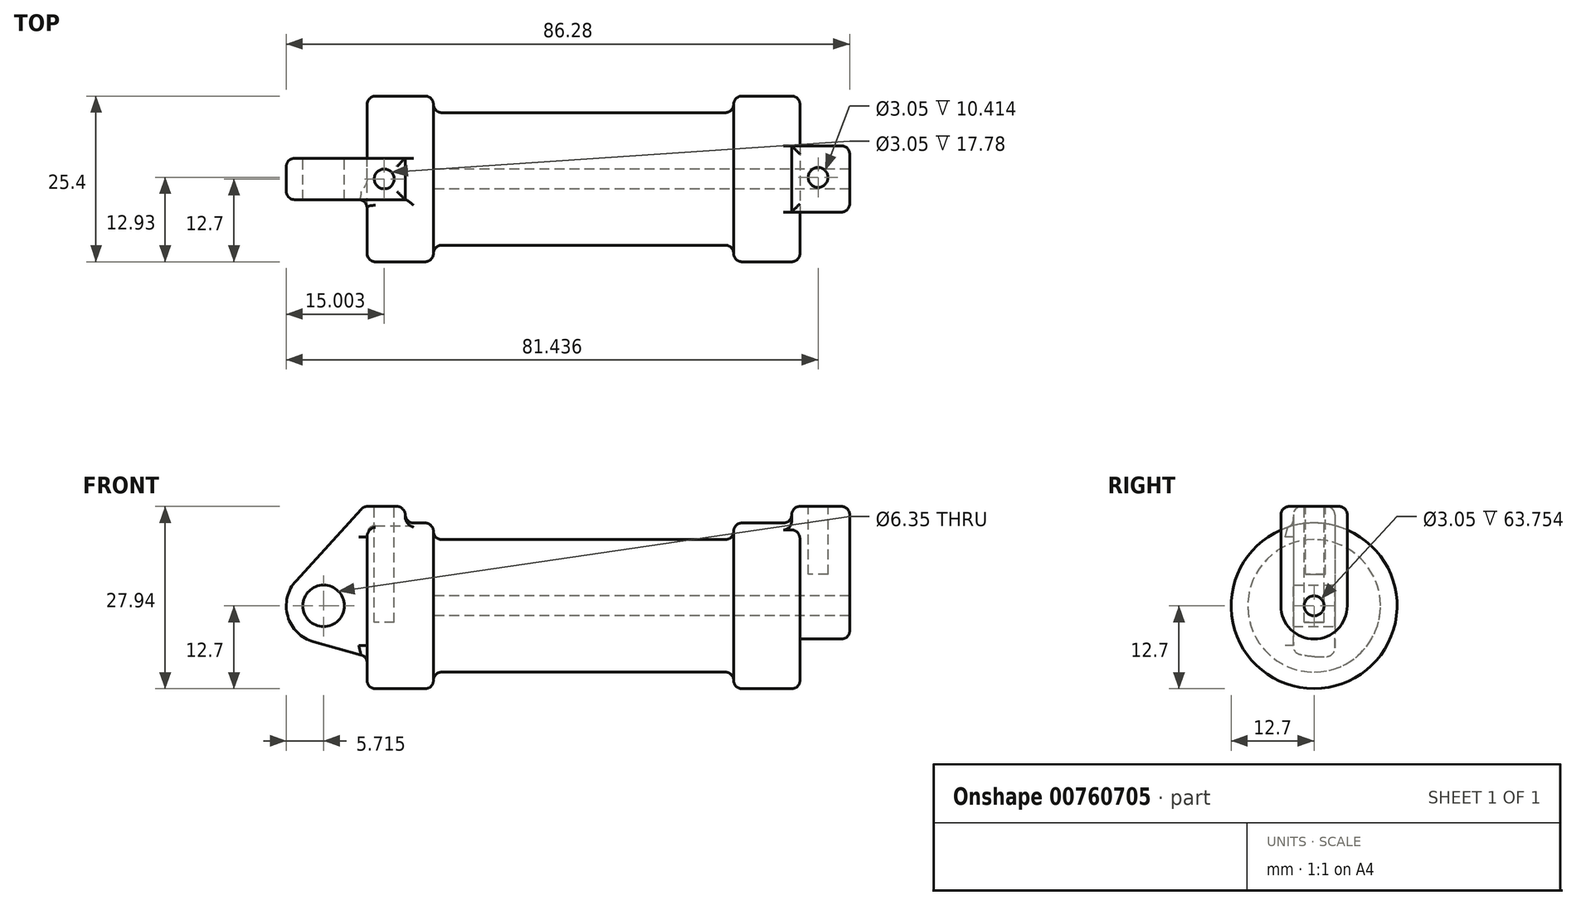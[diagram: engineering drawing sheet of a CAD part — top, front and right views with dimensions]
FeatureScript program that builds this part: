
annotation { "Feature Type Name" : "Feature", "Feature Type Description" : "" }
export const myFeature = defineFeature(function(context is Context, id is Id, definition is map)
    precondition{}
    {
        {
            var Q0;
            Q0=qCreatedBy(makeId("Front.planeOp"),FACE);
            var sketch = newSketch(context, id + "F0", { "sketchPlane" : qUnion([Q0])});
            skLineSegment(sketch, "E0", {"start": v(0, 0) * mm, "end": v(0, 12.7) * mm});
            skLineSegment(sketch, "E1", {"start": v(0, 12.7) * mm, "end": v(10.16, 12.7) * mm});
            skLineSegment(sketch, "E2", {"start": v(10.16, 12.7) * mm, "end": v(10.16, 10.16) * mm});
            skLineSegment(sketch, "E3", {"start": v(10.16, 10.16) * mm, "end": v(56.13, 10.16) * mm});
            skLineSegment(sketch, "E4", {"start": v(56.13, 10.16) * mm, "end": v(56.13, 12.7) * mm});
            skLineSegment(sketch, "E5", {"start": v(56.13, 12.7) * mm, "end": v(66.3, 12.7) * mm});
            skLineSegment(sketch, "E6", {"start": v(66.3, 12.7) * mm, "end": v(66.3, 0) * mm});
            skLineSegment(sketch, "E7", {"start": v(66.3, 0) * mm, "end": v(0, 0) * mm});
            skLineSegment(sketch, "E8", {"start": v(5.84, 15.24) * mm, "end": v(-0.5, 15.24) * mm});
            skLineSegment(sketch, "E9", {"start": v(-0.5, 15.24) * mm, "end": v(-10.88, 3.85) * mm});
            skLineSegment(sketch, "E10", {"start": v(0, 0) * mm, "end": v(-6.65, 0) * mm});
            skCircle(sketch, "E11", {"center": v(-6.65, 0) * mm, "radius": 5.72 * mm});
            skCircle(sketch, "E12", {"center": v(-6.65, 0) * mm, "radius": 3.18 * mm});
            skLineSegment(sketch, "E13", {"start": v(5.84, 15.24) * mm, "end": v(5.84, -9.4) * mm});
            skLineSegment(sketch, "E14", {"start": v(5.84, -9.4) * mm, "end": v(-8.18, -5.5) * mm});
            skSolve(sketch);
        }
        {
            var Q0;
            {var subQ0=sQuery(id+"F0.wireOp",EDGE,"E2");Q0=makeQuery(id+"F0.imprint","IMPRINT",FACE,{"disambiguationData":[TD([[makeQuery(id+"F0.imprint","IMPRINT",EDGE,{"derivedFrom":subQ0}),-1.0]])]});}
            var Q1;
            {var subQ0=sQuery(id+"F0.wireOp",EDGE,"E0");Q1=makeQuery(id+"F0.imprint","IMPRINT",FACE,{"disambiguationData":[TD([[makeQuery(id+"F0.imprint","IMPRINT",EDGE,{"derivedFrom":subQ0}),-1.0]])]});}
            var Q2;
            Q2=sQuery(id+"F0.wireOp",EDGE,"E7");
            revolve(context, id + "F1", {"surfaceOperationType" : NewSurfaceOperationType.NEW, "entities" : qUnion([Q0, Q1]), "axis" : qUnion([Q2]), "revolveType" : RevolveType.FULL});
        }
        {
            var Q0;
            {var subQ5=sQuery(id+"F0.wireOp",EDGE,"E12");Q0=makeQuery(id+"F0.imprint","IMPRINT",FACE,{"disambiguationData":[TD([[makeQuery(id+"F0.imprint","IMPRINT",EDGE,{"derivedFrom":subQ5}),-1.0]])]});}
            var Q1;
            {var subQ0=sQuery(id+"F0.wireOp",EDGE,"E14");Q1=makeQuery(id+"F0.imprint","IMPRINT",FACE,{"disambiguationData":[TD([[makeQuery(id+"F0.imprint","IMPRINT",EDGE,{"derivedFrom":subQ0}),-1.0]])]});}
            var Q2;
            {var subQ0=sQuery(id+"F0.wireOp",EDGE,"E0");Q2=makeQuery(id+"F0.imprint","IMPRINT",FACE,{"disambiguationData":[TD([[makeQuery(id+"F0.imprint","IMPRINT",EDGE,{"derivedFrom":subQ0}),-1.0]])]});}
            var Q3;
            {var subQ1=sQuery(id+"F0.wireOp",EDGE,"E0");Q3=makeQuery(id+"F0.imprint","IMPRINT",FACE,{"disambiguationData":[TD([[makeQuery(id+"F0.imprint","IMPRINT",EDGE,{"derivedFrom":subQ1}),1.0]])]});}
            extrude(context, id + "F2", {"entities" : qUnion([Q0, Q1, Q2, Q3]), "endBound" : BoundingType.SYMMETRIC, "depth" : 6.35 * mm, "offsetDistance" : 25.4 * mm});
        }
        {
            var Q0;
            Q0=makeQuery(id+"F1.opRevolve","SWEPT_FACE",FACE,{"disambiguationData":[OSD([sQuery(id+"F0.wireOp",EDGE,"E6")])]});
            var sketch = newSketch(context, id + "F3", { "sketchPlane" : qUnion([Q0])});
            skCircle(sketch, "E15", {"center": v(0, 0) * mm, "radius": 1.52 * mm});
            skCircle(sketch, "E16", {"center": v(0, 0) * mm, "radius": 5.08 * mm});
            skLineSegment(sketch, "E17", {"start": v(-5.08, 0) * mm, "end": v(-5.08, 15.24) * mm});
            skLineSegment(sketch, "E18", {"start": v(-5.08, 15.24) * mm, "end": v(5.08, 15.24) * mm});
            skLineSegment(sketch, "E19", {"start": v(5.08, 15.24) * mm, "end": v(5.08, 0) * mm});
            skSolve(sketch);
        }
        {
            var Q0;
            {var subQ0=sQuery(id+"F3.wireOp",EDGE,"E18");Q0=makeQuery(id+"F3.imprint","IMPRINT",FACE,{"disambiguationData":[TD([[makeQuery(id+"F3.imprint","IMPRINT",EDGE,{"derivedFrom":subQ0}),-1.0]])]});}
            var Q1;
            {var subQ0=sQuery(id+"F3.wireOp",EDGE,"E17");var subQ1=sQuery(id+"F3.wireOp",EDGE,"E16");var subQ2=makeQuery(id+"F3.imprint","INTERSECT",VERTEX,{"derivedFrom":[subQ1,subQ0]});Q1=makeQuery(id+"F3.imprint","IMPRINT",FACE,{"disambiguationData":[TD([[makeQuery(id+"F3.imprint","IMPRINT",EDGE,{"disambiguationData":[TD([[subQ2,1.0]])],"derivedFrom":subQ1}),-1.0]])]});}
            var Q2;
            Q2=makeQuery(id+"F3.imprint","IMPRINT",FACE,{"disambiguationData":[TD([[makeQuery(id+"F3.imprint","IMPRINT",EDGE,{"derivedFrom":sQuery(id+"F3.wireOp",EDGE,"E15")}),-1.0]])]});
            extrude(context, id + "F4", {"entities" : qUnion([Q0, Q1, Q2]), "operationType" : NewBodyOperationType.ADD, "oppositeDirection" : true, "depth" : 1.27 * mm, "offsetDistance" : 25.4 * mm});
        }
        {
            var Q0;
            Q0=makeQuery(id+"F1.opRevolve","SWEPT_BODY",BODY,{"disambiguationData":[OSD([sQuery(id+"F0.wireOp",EDGE,"E0"),sQuery(id+"F0.wireOp",EDGE,"E1"),sQuery(id+"F0.wireOp",EDGE,"E2"),sQuery(id+"F0.wireOp",EDGE,"E3"),sQuery(id+"F0.wireOp",EDGE,"E4"),sQuery(id+"F0.wireOp",EDGE,"E5"),sQuery(id+"F0.wireOp",EDGE,"E6"),sQuery(id+"F0.wireOp",EDGE,"E7")])]});
            var Q1;
            Q1=makeQuery(id+"F2.opExtrude","SWEPT_BODY",BODY,{"disambiguationData":[OSD([sQuery(id+"F0.wireOp",EDGE,"E8"),sQuery(id+"F0.wireOp",EDGE,"E9"),sQuery(id+"F0.wireOp",EDGE,"E11"),sQuery(id+"F0.wireOp",EDGE,"E12"),sQuery(id+"F0.wireOp",EDGE,"E13"),sQuery(id+"F0.wireOp",EDGE,"E14")])]});
            booleanBodies(context, id + "F5", {"operationType" : BooleanOperationType.UNION, "tools" : qUnion([Q0, Q1])});
        }
        {
            var Q0;
            Q0=makeQuery(id+"F3.imprint","IMPRINT",FACE,{"disambiguationData":[TD([[makeQuery(id+"F3.imprint","IMPRINT",EDGE,{"derivedFrom":sQuery(id+"F3.wireOp",EDGE,"E15")}),-1.0]])]});
            var Q1;
            {var subQ0=sQuery(id+"F3.wireOp",EDGE,"E17");var subQ1=sQuery(id+"F3.wireOp",EDGE,"E16");var subQ2=makeQuery(id+"F3.imprint","INTERSECT",VERTEX,{"derivedFrom":[subQ1,subQ0]});Q1=makeQuery(id+"F3.imprint","IMPRINT",FACE,{"disambiguationData":[TD([[makeQuery(id+"F3.imprint","IMPRINT",EDGE,{"disambiguationData":[TD([[subQ2,1.0]])],"derivedFrom":subQ1}),-1.0]])]});}
            var Q2;
            {var subQ0=sQuery(id+"F3.wireOp",EDGE,"E18");Q2=makeQuery(id+"F3.imprint","IMPRINT",FACE,{"disambiguationData":[TD([[makeQuery(id+"F3.imprint","IMPRINT",EDGE,{"derivedFrom":subQ0}),-1.0]])]});}
            extrude(context, id + "F6", {"entities" : qUnion([Q0, Q1, Q2]), "operationType" : NewBodyOperationType.ADD, "depth" : 7.62 * mm, "offsetDistance" : 25.4 * mm});
        }
        {
            var Q0;
            Q0=makeQuery(id+"F3.imprint","IMPRINT",FACE,{"disambiguationData":[TD([[makeQuery(id+"F3.imprint","IMPRINT",EDGE,{"derivedFrom":sQuery(id+"F3.wireOp",EDGE,"E15")}),1.0]])]});
            var Q1;
            Q1=makeQuery(id+"F1.opRevolve","SWEPT_FACE",FACE,{"disambiguationData":[OSD([sQuery(id+"F0.wireOp",EDGE,"E2")])]});
            extrude(context, id + "F7", {"entities" : qUnion([Q0]), "operationType" : NewBodyOperationType.REMOVE, "endBound" : BoundingType.UP_TO_SURFACE, "oppositeDirection" : true, "depth" : 25.4 * mm, "endBoundEntityFace" : qUnion([Q1]), "offsetDistance" : 25.4 * mm});
        }
        {
            var Q0;
            {var subQ0=sQuery(id+"F3.wireOp",EDGE,"E18");Q0=makeQuery(id+"F6.boolean.opBoolean","MERGE",FACE,{"derivedFrom":[makeQuery(id+"F4.opExtrude","SWEPT_FACE",FACE,{"disambiguationData":[OSD([subQ0])]}),makeQuery(id+"F6.opExtrude","SWEPT_FACE",FACE,{"disambiguationData":[OSD([subQ0])]})]});}
            var sketch = newSketch(context, id + "F8", { "sketchPlane" : qUnion([Q0])});
            skCircle(sketch, "E20", {"center": v(69.07, 0.23) * mm, "radius": 1.52 * mm});
            skSolve(sketch);
        }
        {
            var Q0;
            Q0=makeQuery(id+"F8.imprint","IMPRINT",FACE,{"disambiguationData":[TD([[makeQuery(id+"F8.imprint","IMPRINT",EDGE,{"derivedFrom":sQuery(id+"F8.wireOp",EDGE,"E20")}),1.0]])]});
            extrude(context, id + "F9", {"entities" : qUnion([Q0]), "operationType" : NewBodyOperationType.REMOVE, "oppositeDirection" : true, "depth" : 10.4 * mm, "offsetDistance" : 25.4 * mm});
        }
        {
            var Q0;
            Q0=makeQuery(id+"F2.opExtrude","SWEPT_FACE",FACE,{"disambiguationData":[OSD([sQuery(id+"F0.wireOp",EDGE,"E8")])]});
            var sketch = newSketch(context, id + "F10", { "sketchPlane" : qUnion([Q0])});
            skCircle(sketch, "E21", {"center": v(2.63, 0) * mm, "radius": 1.52 * mm});
            skSolve(sketch);
        }
        {
            var Q0;
            Q0=makeQuery(id+"F10.imprint","IMPRINT",FACE,{"disambiguationData":[TD([[makeQuery(id+"F10.imprint","IMPRINT",EDGE,{"derivedFrom":sQuery(id+"F10.wireOp",EDGE,"E21")}),1.0]])]});
            extrude(context, id + "F11", {"entities" : qUnion([Q0]), "operationType" : NewBodyOperationType.REMOVE, "oppositeDirection" : true, "depth" : 17.78 * mm, "offsetDistance" : 25.4 * mm});
        }
        {
            var Q0;
            Q0=makeQuery(id+"F1.opRevolve","SWEPT_EDGE",EDGE,{"disambiguationData":[OSD([sQuery(id+"F0.wireOp",EDGE,"E2"),sQuery(id+"F0.wireOp",EDGE,"E3")])]});
            var Q1;
            Q1=makeQuery(id+"F1.opRevolve","SWEPT_EDGE",EDGE,{"disambiguationData":[OSD([sQuery(id+"F0.wireOp",EDGE,"E3"),sQuery(id+"F0.wireOp",EDGE,"E4")])]});
            fillet(context, id + "F12", {"entities" : qUnion([Q0, Q1]), "radius" : 1.27 * mm, "tangentPropagation" : true, "allowEdgeOverflow" : false});
        }
        {
            var Q0;
            Q0=makeQuery(id+"F2.opExtrude","CAP_EDGE",EDGE,{"disambiguationData":[OSD([sQuery(id+"F0.wireOp",EDGE,"E9")])],"isStart":false});
            var Q1;
            Q1=makeQuery(id+"F2.opExtrude","SWEPT_EDGE",EDGE,{"disambiguationData":[OSD([sQuery(id+"F0.wireOp",EDGE,"E8"),sQuery(id+"F0.wireOp",EDGE,"E9")])]});
            var Q2;
            Q2=makeQuery(id+"F2.opExtrude","CAP_EDGE",EDGE,{"disambiguationData":[OSD([sQuery(id+"F0.wireOp",EDGE,"E8")])],"isStart":false});
            var Q3;
            Q3=makeQuery(id+"F2.opExtrude","SWEPT_EDGE",EDGE,{"disambiguationData":[OSD([sQuery(id+"F0.wireOp",EDGE,"E8"),sQuery(id+"F0.wireOp",EDGE,"E13")])]});
            var Q4;
            Q4=makeQuery(id+"F2.opExtrude","CAP_EDGE",EDGE,{"disambiguationData":[OSD([sQuery(id+"F0.wireOp",EDGE,"E8")])],"isStart":true});
            var Q5;
            Q5=makeQuery(id+"F2.opExtrude","CAP_EDGE",EDGE,{"disambiguationData":[OSD([sQuery(id+"F0.wireOp",EDGE,"E9")])],"isStart":true});
            var Q6;
            Q6=makeQuery(id+"F5.opBoolean","INTERSECT",EDGE,{"derivedFrom":[makeQuery(id+"F1.opRevolve","SWEPT_FACE",FACE,{"disambiguationData":[OSD([sQuery(id+"F0.wireOp",EDGE,"E1")])]}),makeQuery(id+"F2.opExtrude","SWEPT_FACE",FACE,{"disambiguationData":[OSD([sQuery(id+"F0.wireOp",EDGE,"E13")])]})]});
            var Q7;
            Q7=makeQuery(id+"F1.opRevolve","SWEPT_EDGE",EDGE,{"disambiguationData":[OSD([sQuery(id+"F0.wireOp",EDGE,"E1"),sQuery(id+"F0.wireOp",EDGE,"E2")])]});
            var Q8;
            Q8=makeQuery(id+"F1.opRevolve","SWEPT_EDGE",EDGE,{"disambiguationData":[OSD([sQuery(id+"F0.wireOp",EDGE,"E0"),sQuery(id+"F0.wireOp",EDGE,"E1")])]});
            var Q9;
            Q9=makeQuery(id+"F5.opBoolean","INTERSECT",EDGE,{"derivedFrom":[makeQuery(id+"F1.opRevolve","SWEPT_FACE",FACE,{"disambiguationData":[OSD([sQuery(id+"F0.wireOp",EDGE,"E0")])]}),makeQuery(id+"F2.opExtrude","CAP_FACE",FACE,{"disambiguationData":[OSD([sQuery(id+"F0.wireOp",EDGE,"E8"),sQuery(id+"F0.wireOp",EDGE,"E9"),sQuery(id+"F0.wireOp",EDGE,"E11"),sQuery(id+"F0.wireOp",EDGE,"E12"),sQuery(id+"F0.wireOp",EDGE,"E13"),sQuery(id+"F0.wireOp",EDGE,"E14")])],"isStart":false})]});
            var Q10;
            Q10=makeQuery(id+"F5.opBoolean","INTERSECT",EDGE,{"derivedFrom":[makeQuery(id+"F1.opRevolve","SWEPT_FACE",FACE,{"disambiguationData":[OSD([sQuery(id+"F0.wireOp",EDGE,"E1")])]}),makeQuery(id+"F2.opExtrude","CAP_FACE",FACE,{"disambiguationData":[OSD([sQuery(id+"F0.wireOp",EDGE,"E8"),sQuery(id+"F0.wireOp",EDGE,"E9"),sQuery(id+"F0.wireOp",EDGE,"E11"),sQuery(id+"F0.wireOp",EDGE,"E12"),sQuery(id+"F0.wireOp",EDGE,"E13"),sQuery(id+"F0.wireOp",EDGE,"E14")])],"isStart":false})]});
            fillet(context, id + "F13", {"entities" : qUnion([Q0, Q1, Q2, Q3, Q4, Q5, Q6, Q7, Q8, Q9, Q10]), "radius" : 1.27 * mm, "tangentPropagation" : true, "allowEdgeOverflow" : false});
        }
        {
            var Q0;
            Q0=makeQuery(id+"F1.opRevolve","SWEPT_EDGE",EDGE,{"disambiguationData":[OSD([sQuery(id+"F0.wireOp",EDGE,"E4"),sQuery(id+"F0.wireOp",EDGE,"E5")])]});
            var Q1;
            Q1=makeQuery(id+"F1.opRevolve","SWEPT_EDGE",EDGE,{"disambiguationData":[OSD([sQuery(id+"F0.wireOp",EDGE,"E5"),sQuery(id+"F0.wireOp",EDGE,"E6")])]});
            fillet(context, id + "F14", {"entities" : qUnion([Q0, Q1]), "radius" : 1.27 * mm, "tangentPropagation" : true, "allowEdgeOverflow" : false});
        }
        {
            var Q0;
            Q0=makeQuery(id+"F6.opExtrude","CAP_EDGE",EDGE,{"disambiguationData":[OSD([sQuery(id+"F3.wireOp",EDGE,"E16")])],"isStart":false});
            var Q1;
            Q1=makeQuery(id+"F6.opExtrude","CAP_EDGE",EDGE,{"disambiguationData":[OSD([sQuery(id+"F3.wireOp",EDGE,"E17")])],"isStart":false});
            var Q2;
            Q2=makeQuery(id+"F6.opExtrude","CAP_EDGE",EDGE,{"disambiguationData":[OSD([sQuery(id+"F3.wireOp",EDGE,"E18")])],"isStart":false});
            var Q3;
            {var subQ0=sQuery(id+"F3.wireOp",EDGE,"E19");var subQ1=sQuery(id+"F3.wireOp",EDGE,"E18");Q3=makeQuery(id+"F6.boolean.opBoolean","MERGE",EDGE,{"derivedFrom":[makeQuery(id+"F4.opExtrude","SWEPT_EDGE",EDGE,{"disambiguationData":[OSD([subQ1,subQ0])]}),makeQuery(id+"F6.opExtrude","SWEPT_EDGE",EDGE,{"disambiguationData":[OSD([subQ1,subQ0])]})]});}
            var Q4;
            {var subQ0=sQuery(id+"F3.wireOp",EDGE,"E18");var subQ1=sQuery(id+"F3.wireOp",EDGE,"E17");Q4=makeQuery(id+"F6.boolean.opBoolean","MERGE",EDGE,{"derivedFrom":[makeQuery(id+"F4.opExtrude","SWEPT_EDGE",EDGE,{"disambiguationData":[OSD([subQ1,subQ0])]}),makeQuery(id+"F6.opExtrude","SWEPT_EDGE",EDGE,{"disambiguationData":[OSD([subQ1,subQ0])]})]});}
            var Q5;
            Q5=makeQuery(id+"F4.opExtrude","CAP_EDGE",EDGE,{"disambiguationData":[OSD([sQuery(id+"F3.wireOp",EDGE,"E18")])],"isStart":false});
            var Q6;
            Q6=makeQuery(id+"F4.boolean.opBoolean","INTERSECT",EDGE,{"derivedFrom":[makeQuery(id+"F1.opRevolve","SWEPT_FACE",FACE,{"disambiguationData":[OSD([sQuery(id+"F0.wireOp",EDGE,"E5")])]}),makeQuery(id+"F4.opExtrude","CAP_FACE",FACE,{"disambiguationData":[OSD([sQuery(id+"F3.wireOp",EDGE,"E15"),sQuery(id+"F3.wireOp",EDGE,"E16"),sQuery(id+"F3.wireOp",EDGE,"E17"),sQuery(id+"F3.wireOp",EDGE,"E18"),sQuery(id+"F3.wireOp",EDGE,"E19")])],"isStart":false})]});
            var Q7;
            Q7=makeQuery(id+"F6.opExtrude","CAP_EDGE",EDGE,{"disambiguationData":[OSD([sQuery(id+"F3.wireOp",EDGE,"E16")])],"isStart":true});
            var Q8;
            Q8=makeQuery(id+"F6.opExtrude","CAP_EDGE",EDGE,{"disambiguationData":[OSD([sQuery(id+"F3.wireOp",EDGE,"E19")])],"isStart":true});
            var Q9;
            Q9=makeQuery(id+"F6.opExtrude","CAP_EDGE",EDGE,{"disambiguationData":[OSD([sQuery(id+"F3.wireOp",EDGE,"E17")])],"isStart":true});
            fillet(context, id + "F15", {"entities" : qUnion([Q0, Q1, Q2, Q3, Q4, Q5, Q6, Q7, Q8, Q9]), "radius" : 1.27 * mm, "tangentPropagation" : true, "allowEdgeOverflow" : false});
        }
    });
